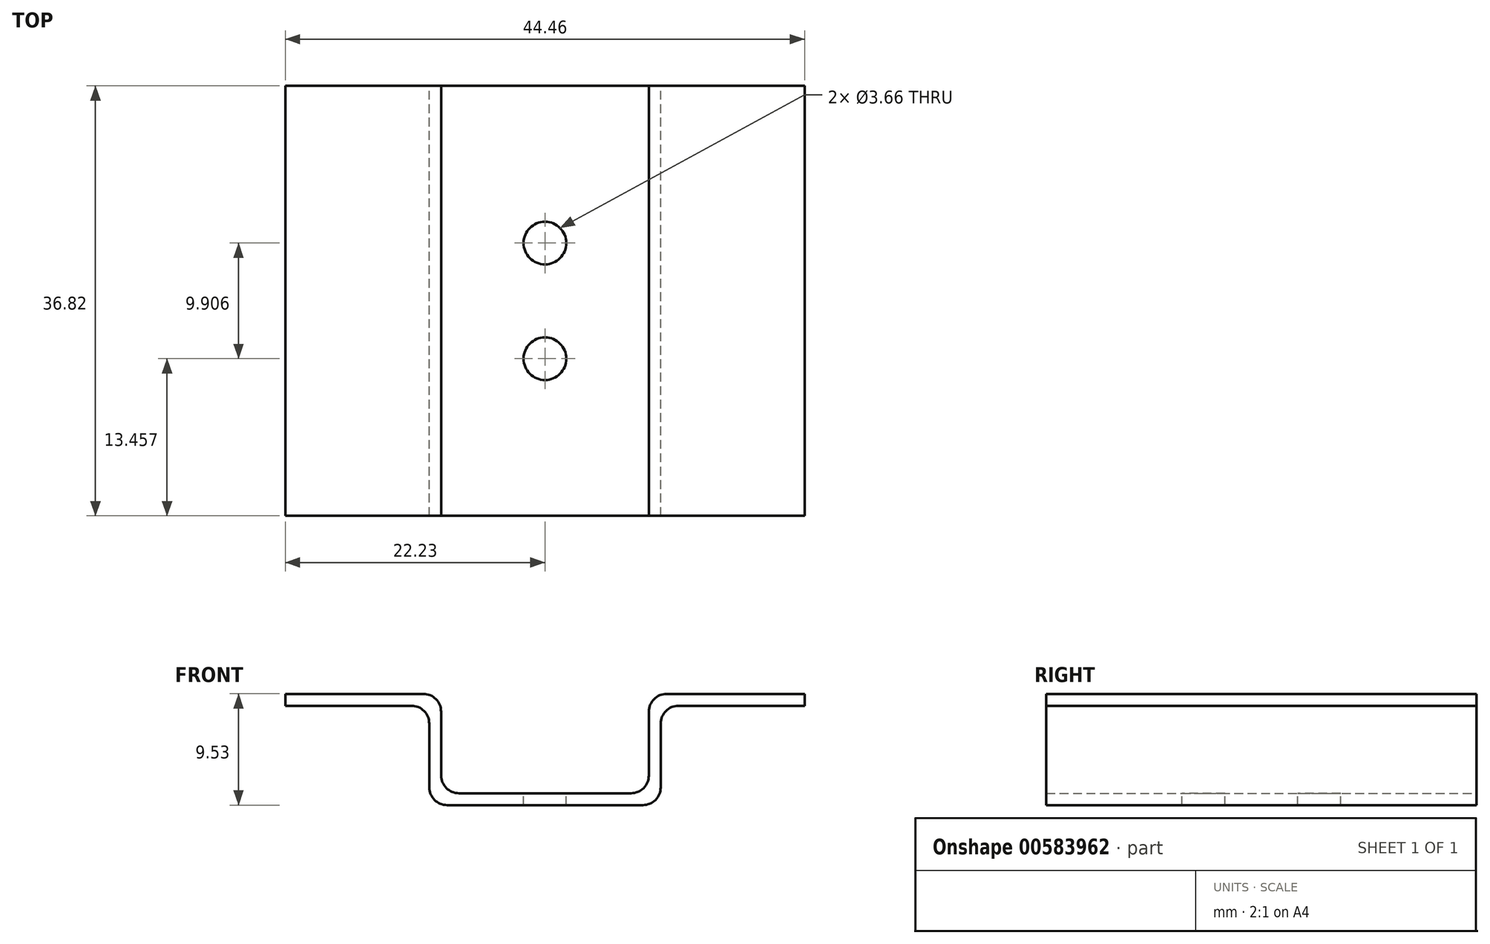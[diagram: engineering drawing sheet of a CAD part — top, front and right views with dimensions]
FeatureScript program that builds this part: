
annotation { "Feature Type Name" : "Feature", "Feature Type Description" : "" }
export const myFeature = defineFeature(function(context is Context, id is Id, definition is map)
    precondition{}
    {
        {
            var Q0;
            Q0=qCreatedBy(makeId("Front.planeOp"),FACE);
            var sketch = newSketch(context, id + "F0", { "sketchPlane" : qUnion([Q0])});
            skLineSegment(sketch, "E0", {"start": v(0, 0) * mm, "end": v(-8.38, 0) * mm});
            skLineSegment(sketch, "E1", {"start": v(-9.9, 1.52) * mm, "end": v(-9.9, 6.99) * mm});
            skLineSegment(sketch, "E2", {"start": v(-11.43, 8.5) * mm, "end": v(-22.23, 8.5) * mm});
            skLineSegment(sketch, "E3", {"start": v(-22.23, 8.5) * mm, "end": v(-22.23, 9.53) * mm});
            skLineSegment(sketch, "E4", {"start": v(-22.23, 9.53) * mm, "end": v(-10.41, 9.53) * mm});
            skLineSegment(sketch, "E5", {"start": v(-8.89, 8) * mm, "end": v(-8.89, 2.54) * mm});
            skLineSegment(sketch, "E6", {"start": v(-7.37, 1.02) * mm, "end": v(0, 1.02) * mm});
            skLineSegment(sketch, "E7", {"start": v(-9.9, 4.25) * mm, "end": v(-8.89, 4.25) * mm, "construction": true});
            skLineSegment(sketch, "E8", {"start": v(-4.44, 1.02) * mm, "end": v(-4.44, 0) * mm, "construction": true});
            skLineSegment(sketch, "E9.MirrorCS", {"start": v(0, 0) * mm, "end": v(8.38, 0) * mm});
            skLineSegment(sketch, "E10.MirrorCS", {"start": v(9.9, 1.52) * mm, "end": v(9.9, 6.99) * mm});
            skLineSegment(sketch, "E11.MirrorCS", {"start": v(22.23, 9.53) * mm, "end": v(10.41, 9.52) * mm});
            skLineSegment(sketch, "E12.MirrorCS", {"start": v(9.9, 4.25) * mm, "end": v(8.89, 4.25) * mm, "construction": true});
            skLineSegment(sketch, "E13.MirrorCS", {"start": v(4.44, 1.02) * mm, "end": v(4.44, 0) * mm, "construction": true});
            skLineSegment(sketch, "E14.MirrorCS", {"start": v(8.89, 8) * mm, "end": v(8.89, 2.54) * mm});
            skLineSegment(sketch, "E15.MirrorCS", {"start": v(22.23, 8.5) * mm, "end": v(22.23, 9.53) * mm});
            skLineSegment(sketch, "E16.MirrorCS", {"start": v(7.37, 1.02) * mm, "end": v(0, 1.02) * mm});
            skLineSegment(sketch, "E17.MirrorCS", {"start": v(11.43, 8.5) * mm, "end": v(22.23, 8.5) * mm});
            skPoint(sketch, "E18.visualSharp", {"position": v(-8.89, 9.53) * mm});
            skArc(sketch, "E18.filletArc", {"start": v(-8.89, 8) * mm, "mid": v(-9.34, 9.08) * mm, "end": v(-10.41, 9.53) * mm});
            skPoint(sketch, "E19.visualSharp", {"position": v(-9.9, 8.5) * mm});
            skArc(sketch, "E19.filletArc", {"start": v(-9.9, 6.99) * mm, "mid": v(-10.35, 8.06) * mm, "end": v(-11.43, 8.5) * mm});
            skPoint(sketch, "E20.visualSharp", {"position": v(9.9, 8.5) * mm});
            skArc(sketch, "E20.filletArc", {"start": v(11.43, 8.5) * mm, "mid": v(10.35, 8.06) * mm, "end": v(9.9, 6.99) * mm});
            skPoint(sketch, "E21.visualSharp", {"position": v(8.89, 9.52) * mm});
            skArc(sketch, "E21.filletArc", {"start": v(10.41, 9.53) * mm, "mid": v(9.34, 9.08) * mm, "end": v(8.9, 8) * mm});
            skPoint(sketch, "E22.visualSharp", {"position": v(-8.89, 1.02) * mm});
            skArc(sketch, "E22.filletArc", {"start": v(-8.89, 2.54) * mm, "mid": v(-8.44, 1.46) * mm, "end": v(-7.37, 1.02) * mm});
            skPoint(sketch, "E23.visualSharp", {"position": v(-9.9, 0) * mm});
            skArc(sketch, "E23.filletArc", {"start": v(-9.9, 1.52) * mm, "mid": v(-9.46, 0.45) * mm, "end": v(-8.38, 0) * mm});
            skPoint(sketch, "E24.visualSharp", {"position": v(8.89, 1.02) * mm});
            skArc(sketch, "E24.filletArc", {"start": v(7.37, 1.02) * mm, "mid": v(8.44, 1.46) * mm, "end": v(8.89, 2.54) * mm});
            skPoint(sketch, "E25.visualSharp", {"position": v(9.9, 0) * mm});
            skArc(sketch, "E25.filletArc", {"start": v(8.38, 0) * mm, "mid": v(9.46, 0.45) * mm, "end": v(9.9, 1.52) * mm});
            skSolve(sketch);
        }
        {
            var Q0;
            Q0 = qSketchRegion(id + "F0", true);
            extrude(context, id + "F1", {"entities" : qUnion([Q0]), "endBound" : BoundingType.SYMMETRIC, "depth" : 36.83 * mm, "offsetDistance" : 25.4 * mm});
        }
        {
            var Q0;
            Q0=makeQuery(id+"F1.opExtrude","SWEPT_FACE",FACE,{"disambiguationData":[OSD([sQuery(id+"F0.wireOp",EDGE,"E6"),sQuery(id+"F0.wireOp",EDGE,"E16.MirrorCS")])]});
            var sketch = newSketch(context, id + "F2", { "sketchPlane" : qUnion([Q0])});
            skCircle(sketch, "E26", {"center": v(0, -4.95) * mm, "radius": 1.83 * mm});
            skCircle(sketch, "E27.MirrorC", {"center": v(0, 4.95) * mm, "radius": 1.83 * mm});
            skSolve(sketch);
        }
        {
            var Q0;
            Q0 = qSketchRegion(id + "F2", true);
            extrude(context, id + "F3", {"entities" : qUnion([Q0]), "operationType" : NewBodyOperationType.REMOVE, "oppositeDirection" : true, "depth" : 25.4 * mm, "offsetDistance" : 25.4 * mm});
        }
    });
